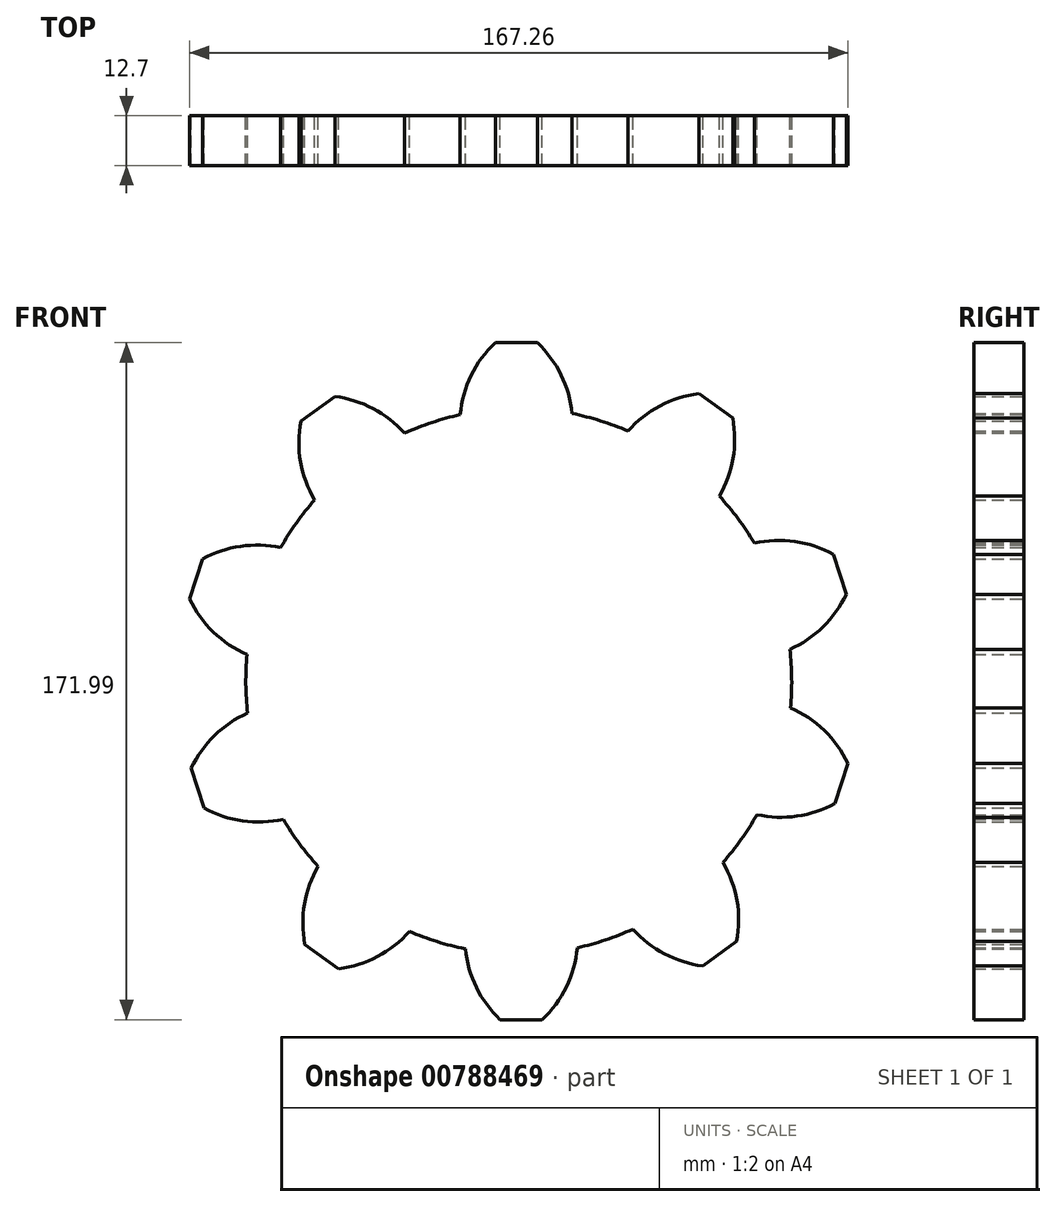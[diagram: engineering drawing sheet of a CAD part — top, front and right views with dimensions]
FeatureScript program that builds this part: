
annotation { "Feature Type Name" : "Feature", "Feature Type Description" : "" }
export const myFeature = defineFeature(function(context is Context, id is Id, definition is map)
    precondition{}
    {
        {
            var Q0;
            Q0=qCreatedBy(makeId("Front.planeOp"),FACE);
            var sketch = newSketch(context, id + "F0", { "sketchPlane" : qUnion([Q0])});
            skArc(sketch, "E0", {"start": v(50.92, 39.38) * mm, "mid": v(48.58, 50.77) * mm, "end": v(41.91, 60.3) * mm});
            skArc(sketch, "E1", {"start": v(31.24, 60.3) * mm, "mid": v(24.56, 50.8) * mm, "end": v(22.2, 39.42) * mm});
            skLineSegment(sketch, "E2", {"start": v(31.24, 60.3) * mm, "end": v(41.91, 60.3) * mm});
            skLineSegment(sketch, "E3", {"start": v(22.2, 39.42) * mm, "end": v(50.92, 39.38) * mm});
            skSolve(sketch);
        }
        {
            var Q0;
            Q0=qCreatedBy(makeId("Front.planeOp"),FACE);
            var sketch = newSketch(context, id + "F1", { "sketchPlane" : qUnion([Q0])});
            skCircle(sketch, "E4", {"center": v(37.2, -25.7) * mm, "radius": 69.35 * mm});
            skSolve(sketch);
        }
        {
            var Q0;
            Q0=makeQuery(id+"F0.imprint","IMPRINT",FACE,{"disambiguationData":[TD([[makeQuery(id+"F0.imprint","IMPRINT",EDGE,{"derivedFrom":sQuery(id+"F0.wireOp",EDGE,"E0")}),1.0]])]});
            extrude(context, id + "F2", {"entities" : qUnion([Q0]), "depth" : 12.7 * mm, "offsetDistance" : 25.4 * mm});
        }
        {
            var Q0;
            Q0=makeQuery(id+"F1.imprint","IMPRINT",FACE,{"disambiguationData":[TD([[makeQuery(id+"F1.imprint","IMPRINT",EDGE,{"derivedFrom":sQuery(id+"F1.wireOp",EDGE,"E4")}),1.0]])]});
            extrude(context, id + "F3", {"entities" : qUnion([Q0]), "operationType" : NewBodyOperationType.ADD, "depth" : 12.7 * mm, "offsetDistance" : 25.4 * mm});
        }
        {
            var Q0;
            Q0=makeQuery(id+"F2.opExtrude","SWEPT_BODY",BODY,{"disambiguationData":[OSD([sQuery(id+"F0.wireOp",EDGE,"E0"),sQuery(id+"F0.wireOp",EDGE,"E1"),sQuery(id+"F0.wireOp",EDGE,"E2"),sQuery(id+"F0.wireOp",EDGE,"E3")])]});
            var Q1;
            Q1=makeQuery(id+"F3.opExtrude","CAP_EDGE",EDGE,{"disambiguationData":[OSD([sQuery(id+"F1.wireOp",EDGE,"E4")])],"isStart":true});
            circularPattern(context, id + "F4", {"operationType" : NewBodyOperationType.ADD, "entities" : qUnion([Q0]), "axis" : qUnion([Q1]), "angle" : 360 * degree, "instanceCount" : 10, "equalSpace" : true});
        }
    });
